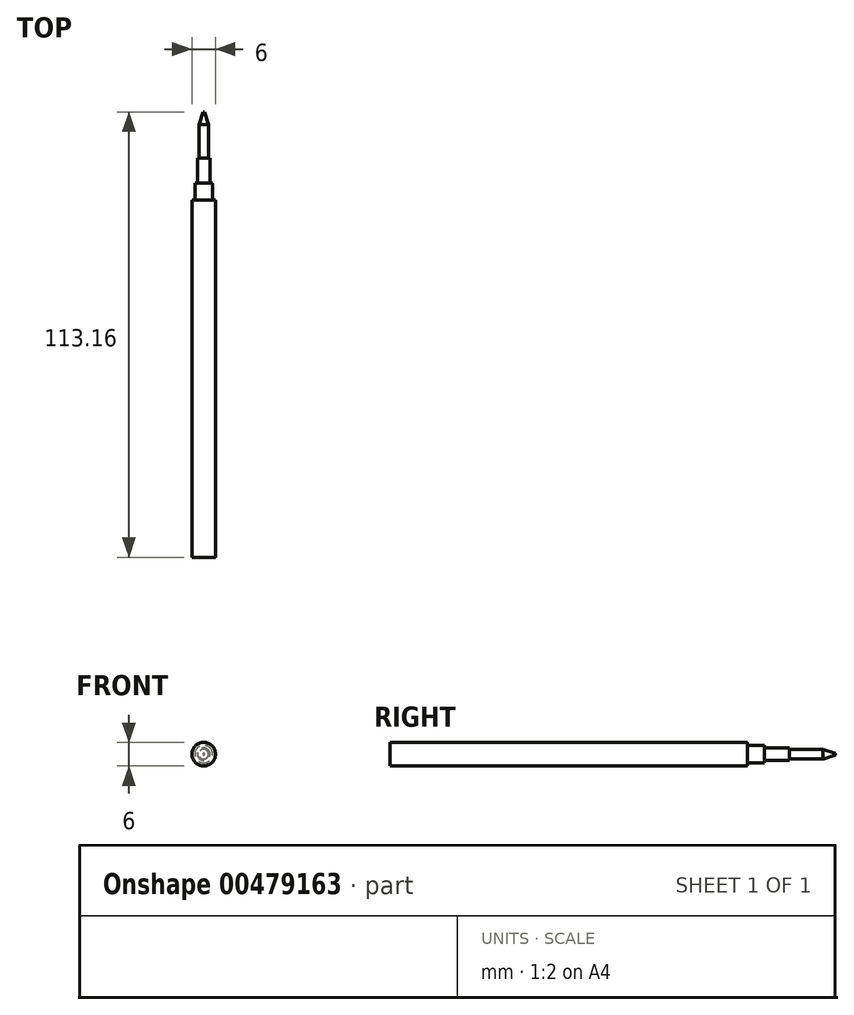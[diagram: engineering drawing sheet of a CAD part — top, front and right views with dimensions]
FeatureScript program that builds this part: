
annotation { "Feature Type Name" : "Feature", "Feature Type Description" : "" }
export const myFeature = defineFeature(function(context is Context, id is Id, definition is map)
    precondition{}
    {
        {
            var Q0;
            Q0=qCreatedBy(makeId("Front.planeOp"),FACE);
            var sketch = newSketch(context, id + "F0", { "sketchPlane" : qUnion([Q0])});
            skCircle(sketch, "E0", {"center": v(0, 0) * mm, "radius": 1.24 * mm});
            skSolve(sketch);
        }
        {
            var Q0;
            Q0 = qSketchRegion(id + "F0", true);
            extrude(context, id + "F1", {"entities" : qUnion([Q0]), "depth" : 11.68 * mm});
        }
        {
            var Q0;
            Q0=makeQuery(id+"F1.opExtrude","CAP_EDGE",EDGE,{"disambiguationData":[OSD([sQuery(id+"F0.wireOp",EDGE,"E0")])],"isStart":true});
            chamfer(context, id + "F2", {"entities" : qUnion([Q0]), "chamferType" : ChamferType.TWO_OFFSETS, "width1" : 3.17 * mm, "oppositeDirection" : false, "width2" : 1.02 * mm, "tangentPropagation" : true});
        }
        {
            var Q0;
            Q0=makeQuery(id+"F1.opExtrude","CAP_FACE",FACE,{"disambiguationData":[OSD([sQuery(id+"F0.wireOp",EDGE,"E0")])],"isStart":false});
            var sketch = newSketch(context, id + "F3", { "sketchPlane" : qUnion([Q0])});
            skCircle(sketch, "E1", {"center": v(0, 0) * mm, "radius": 1.59 * mm});
            skSolve(sketch);
        }
        {
            var Q0;
            Q0 = qSketchRegion(id + "F3", true);
            extrude(context, id + "F4", {"entities" : qUnion([Q0]), "operationType" : NewBodyOperationType.ADD, "depth" : 6.35 * mm});
        }
        {
            var Q0;
            Q0=makeQuery(id+"F4.opExtrude","CAP_FACE",FACE,{"disambiguationData":[OSD([sQuery(id+"F3.wireOp",EDGE,"E1")])],"isStart":false});
            var sketch = newSketch(context, id + "F5", { "sketchPlane" : qUnion([Q0])});
            skCircle(sketch, "E2", {"center": v(0, 0) * mm, "radius": 2.25 * mm});
            skSolve(sketch);
        }
        {
            var Q0;
            Q0 = qSketchRegion(id + "F5", true);
            extrude(context, id + "F6", {"entities" : qUnion([Q0]), "depth" : 4.32 * mm});
        }
        {
            var Q0;
            Q0=makeQuery(id+"F6.opExtrude","CAP_FACE",FACE,{"disambiguationData":[OSD([sQuery(id+"F5.wireOp",EDGE,"E2")])],"isStart":false});
            var sketch = newSketch(context, id + "F7", { "sketchPlane" : qUnion([Q0])});
            skCircle(sketch, "E3", {"center": v(0, 0) * mm, "radius": 3 * mm});
            skSolve(sketch);
        }
        {
            var Q0;
            Q0 = qSketchRegion(id + "F7", true);
            extrude(context, id + "F8", {"entities" : qUnion([Q0]), "operationType" : NewBodyOperationType.ADD, "depth" : 90.8 * mm});
        }
    });
